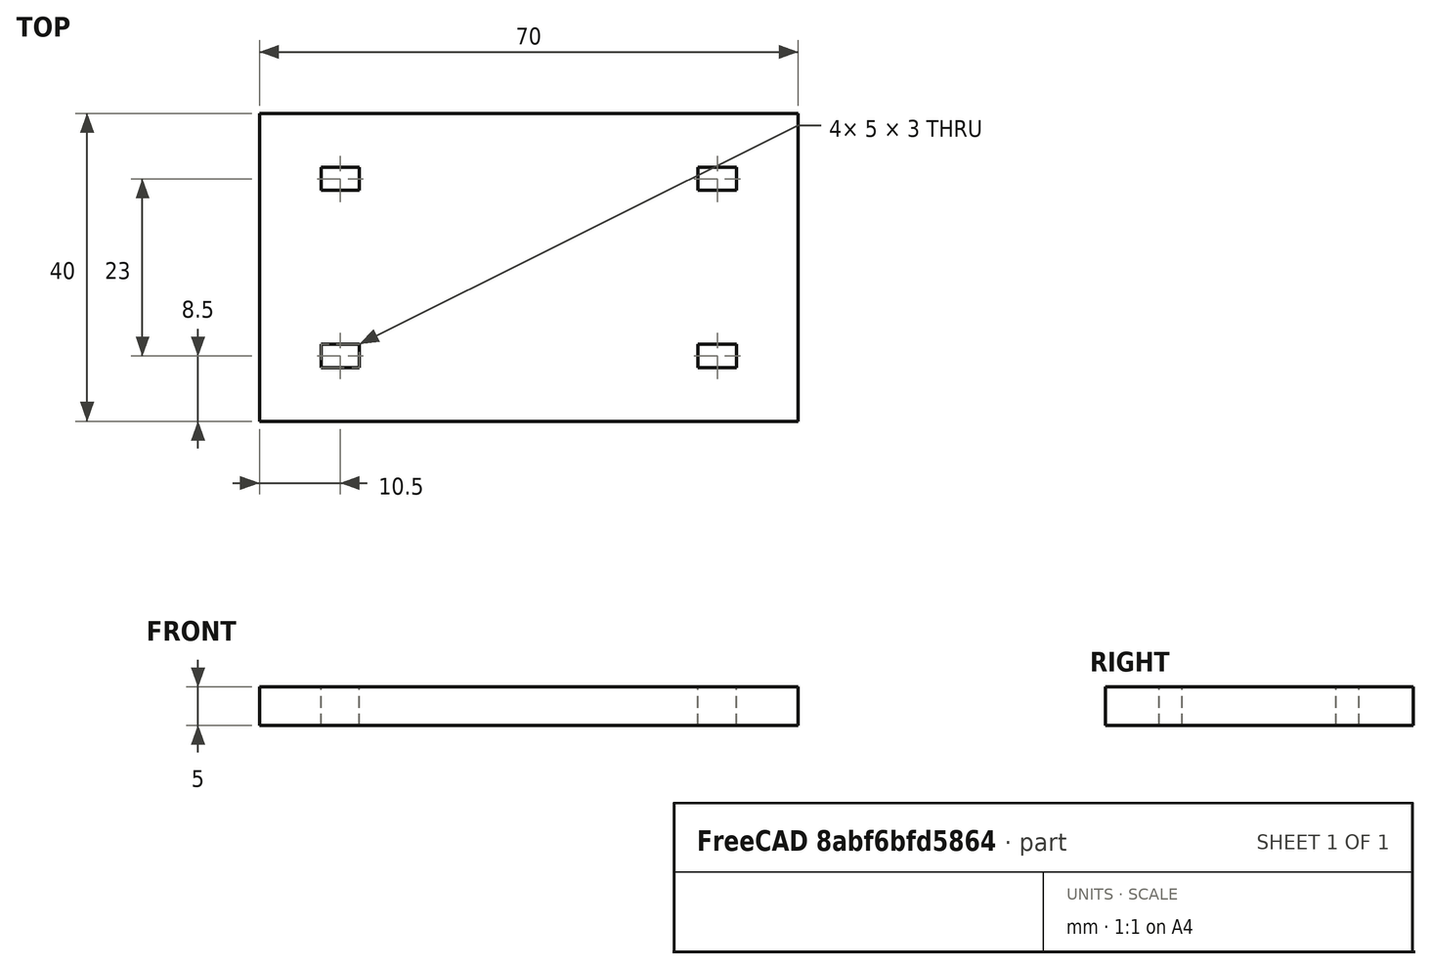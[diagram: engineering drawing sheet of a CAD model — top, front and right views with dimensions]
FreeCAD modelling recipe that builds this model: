
FCSTD DOCUMENT  (FreeCAD 0.17R13509 (Git))
Label: BearingHolder
License: All rights reserved
LicenseURL: http://en.wikipedia.org/wiki/All_rights_reserved
objects: Sketcher::SketchObject×1, PartDesign::Pad×1, PartDesign::Body×1
note: 4 computed .brp shape members not serialized (recipe doc carries the construction recipe); baked Part::Feature solids carry a one-line shape summary decoded from their .brp

FEATURE [Sketcher::SketchObject] Sketch
  MapMode = 5
  Support = -> [XY_Plane]
  sketch-geometry (32):
    g0: LineSegment StartX=-35 StartY=20 StartZ=0 EndX=35 EndY=20 EndZ=0
    g1: LineSegment StartX=35 StartY=20 StartZ=0 EndX=35 EndY=-20 EndZ=0
    g2: LineSegment StartX=35 StartY=-20 StartZ=0 EndX=-35 EndY=-20 EndZ=0
    g3: LineSegment StartX=-35 StartY=-20 StartZ=0 EndX=-35 EndY=20 EndZ=0
    g4: LineSegment [constr] StartX=-25 StartY=20 StartZ=0 EndX=-25 EndY=-20 EndZ=0
    g5: LineSegment [constr] StartX=25 StartY=20 StartZ=0 EndX=25 EndY=-20 EndZ=0
    g6: LineSegment [constr] StartX=-35 StartY=-15 StartZ=0 EndX=35 EndY=-15 EndZ=0
    g7: LineSegment [constr] StartX=35 StartY=15 StartZ=0 EndX=-35 EndY=15 EndZ=0
    g8: LineSegment StartX=-27.5 StartY=16.5 StartZ=0 EndX=-22.5 EndY=16.5 EndZ=0
    g9: LineSegment StartX=-22.5 StartY=16.5 StartZ=0 EndX=-22.5 EndY=13.5 EndZ=0
    g10: LineSegment StartX=-22.5 StartY=13.5 StartZ=0 EndX=-27.5 EndY=13.5 EndZ=0
    g11: LineSegment StartX=-27.5 StartY=13.5 StartZ=0 EndX=-27.5 EndY=16.5 EndZ=0
    g12: LineSegment StartX=22.5 StartY=16.5 StartZ=0 EndX=27.5 EndY=16.5 EndZ=0
    g13: LineSegment StartX=27.5 StartY=16.5 StartZ=0 EndX=27.5 EndY=13.5 EndZ=0
    g14: LineSegment StartX=27.5 StartY=13.5 StartZ=0 EndX=22.5 EndY=13.5 EndZ=0
    g15: LineSegment StartX=22.5 StartY=13.5 StartZ=0 EndX=22.5 EndY=16.5 EndZ=0
    g16: LineSegment StartX=22.5 StartY=-13.5 StartZ=0 EndX=27.5 EndY=-13.5 EndZ=0
    g17: LineSegment StartX=27.5 StartY=-13.5 StartZ=0 EndX=27.5 EndY=-16.5 EndZ=0
    g18: LineSegment StartX=27.5 StartY=-16.5 StartZ=0 EndX=22.5 EndY=-16.5 EndZ=0
    g19: LineSegment StartX=22.5 StartY=-16.5 StartZ=0 EndX=22.5 EndY=-13.5 EndZ=0
    g20: LineSegment StartX=-27.5 StartY=-13.5 StartZ=0 EndX=-22.5 EndY=-13.5 EndZ=0
    g21: LineSegment StartX=-22.5 StartY=-13.5 StartZ=0 EndX=-22.5 EndY=-16.5 EndZ=0
    g22: LineSegment StartX=-22.5 StartY=-16.5 StartZ=0 EndX=-27.5 EndY=-16.5 EndZ=0
    g23: LineSegment StartX=-27.5 StartY=-16.5 StartZ=0 EndX=-27.5 EndY=-13.5 EndZ=0
    g24: LineSegment StartX=-31 StartY=1.5 StartZ=0 EndX=-19 EndY=1.5 EndZ=0
    g25: LineSegment StartX=-19 StartY=1.5 StartZ=0 EndX=-19 EndY=-1.5 EndZ=0
    g26: LineSegment StartX=-19 StartY=-1.5 StartZ=0 EndX=-31 EndY=-1.5 EndZ=0
    g27: LineSegment StartX=-31 StartY=-1.5 StartZ=0 EndX=-31 EndY=1.5 EndZ=0
    g28: LineSegment StartX=19 StartY=1.5 StartZ=0 EndX=31 EndY=1.5 EndZ=0
    g29: LineSegment StartX=31 StartY=1.5 StartZ=0 EndX=31 EndY=-1.5 EndZ=0
    g30: LineSegment StartX=31 StartY=-1.5 StartZ=0 EndX=19 EndY=-1.5 EndZ=0
    g31: LineSegment StartX=19 StartY=-1.5 StartZ=0 EndX=19 EndY=1.5 EndZ=0
  constraints (94):
    c: Coincident(g0,g1)
    c: Coincident(g1,g2)
    c: Coincident(g2,g3)
    c: Coincident(g3,g0)
    c: Horizontal(g2)
    c: Vertical(g1)
    c: Symmetric(g0,g0,g-2)
    c: Symmetric(g2,g0,g-1)
    c: DistanceX(g0,g0) = 70
    c: DistanceY(g3,g3) = 40
    c: PointOnObject(g4,g0)
    c: PointOnObject(g4,g2)
    c: PointOnObject(g5,g0)
    c: PointOnObject(g5,g2)
    c: PointOnObject(g6,g3)
    c: PointOnObject(g6,g1)
    c: PointOnObject(g7,g3)
    c: Symmetric(g4,g5,g-2)
    c: Symmetric(g7,g6,g-1)
    c: PointOnObject(g7,g1)
    c: DistanceY(g6,g7) = 30
    c: DistanceX(g4,g5) = 50
    c: Coincident(g8,g9)
    c: Coincident(g9,g10)
    c: Coincident(g10,g11)
    c: Coincident(g11,g8)
    c: Horizontal(g8)
    c: Horizontal(g10)
    c: Vertical(g9)
    c: Vertical(g11)
    c: Coincident(g12,g13)
    c: Coincident(g13,g14)
    c: Coincident(g14,g15)
    c: Coincident(g15,g12)
    c: Horizontal(g12)
    c: Horizontal(g14)
    c: Vertical(g13)
    c: Vertical(g15)
    c: Coincident(g16,g17)
    c: Coincident(g17,g18)
    c: Coincident(g18,g19)
    c: Coincident(g19,g16)
    c: Horizontal(g16)
    c: Horizontal(g18)
    c: Vertical(g17)
    c: Vertical(g19)
    c: Coincident(g20,g21)
    c: Coincident(g21,g22)
    c: Coincident(g22,g23)
    c: Coincident(g23,g20)
    c: Horizontal(g20)
    c: Horizontal(g22)
    c: Vertical(g21)
    c: Vertical(g23)
    c: Symmetric(g20,g20,g4)
    c: Symmetric(g20,g22,g6)
    c: Symmetric(g8,g8,g4)
    c: Symmetric(g10,g8,g7)
    c: Symmetric(g12,g12,g5)
    c: Symmetric(g12,g14,g7)
    c: Symmetric(g16,g16,g5)
    c: Symmetric(g18,g16,g6)
    c: DistanceX(g8,g8) = 5
    c: DistanceY(g10,g8) = 3
    c: Equal(g8,g12)
    c: Equal(g12,g16)
    c: Equal(g16,g20)
    c: Equal(g11,g23)
    c: Equal(g23,g19)
    c: Equal(g19,g15)
    c: Coincident(g24,g25)
    c: Coincident(g25,g26)
    c: Coincident(g26,g27)
    c: Coincident(g27,g24)
    c: Horizontal(g24)
    c: Horizontal(g26)
    c: Vertical(g25)
    c: Vertical(g27)
    c: Coincident(g28,g29)
    c: Coincident(g29,g30)
    c: Coincident(g30,g31)
    c: Coincident(g31,g28)
    c: Horizontal(g28)
    c: Horizontal(g30)
    c: Vertical(g29)
    c: Vertical(g31)
    c: Symmetric(g24,g24,g4)
    c: Symmetric(g28,g28,g5)
    c: Symmetric(g24,g26,g-1)
    c: Symmetric(g28,g30,g-1)
    c: DistanceX(g24,g24) = 12
    c: Equal(g24,g28)
    c: Equal(g27,g31)
    c: DistanceY(g27,g27) = 3
FEATURE [PartDesign::Pad] Pad
  Length = 5
  Length2 = 100
  Profile = -> Sketch
  Refine = true
  Type = 0
FEATURE [PartDesign::Body] Body
  Group = -> [Sketch,Pad]
  Origin = -> Origin
  Tip = -> Pad
